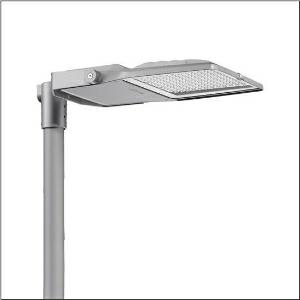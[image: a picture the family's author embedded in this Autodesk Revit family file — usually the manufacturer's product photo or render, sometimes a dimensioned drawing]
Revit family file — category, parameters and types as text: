
# Revit family: floodlight_fl_21_iq_midi___pl43_5xa7781e4a3a_24f4
name_source: partatom
category: Lighting Fixtures
units: mm (PartAtom-declared; Revit-internal decimal feet)

## family parameters
Cut with Voids When Loaded = No
Host = Face
Light Source = No
Part Type = Normal
Room Calculation Point = No
Round Connector Dimension = Use Diameter
Shared = No

## types (1)
- --- (1 x LED, 28730 lm, 208.1 W, 4000K)
    Apparent Load = 208 VA
    CIE Flux Codes = 27 78 99 100 100
    Color Rendering = 70
    Color Temperature = 4000K
    Default Elevation = 1800 mm
    Description = Floodlight FL 21 iQ midi, floodlight, primary light control with lens, of PMMA, primary optical cover: protective disc, of toughened safety glass, transparent, light distribution: PL43, light emission: direct distribution, installation type: surface-mounted, LED, High Power LED, rated luminous flux: 28.730lm, luminous efficacy: 138lm/W, light colour: 740, colour temperature: 4000K, control gear: iQ Comfort/DALI, control: optimised constant luminous flux control (CLO 2.0), Desk-Remote (wireless, voltage-free reading and setting of iQ features in the workshop via application-optimized NFC function/RFID function), Light-Fading, Smart-Wire, Night-Set, Lumen-Switch, Temp-Guard, Auto-Match, with terminal, 6-pole, mains connection: 220..240V, AC, 50/60Hz, start of lifetime: 208W, end of service life: 227W, reduction: 90W, luminaire housing, of diecast aluminium, powder-coated, Siteco® metallic grey (DB 702S), corrosivity category C5 mid according to DIN EN ISO 12944, suitable for swimming pools, chlorine-resistant, sealing non-destructively replaceable, please order mast flange separately, mast bracket, of steel, galvanised, powder-coated, Siteco® metallic grey (DB 702S), protection rating (complete): IP66, insulation class (complete): insulation class II (safety insulation), certification: CE, ENEC, VDE, protection symbol: D, impact resistance: IK08, permissible operating ambient temperature: -40..+40°C, permissible operating ambient temperature for outdoor applications: -40..+50°C, standard: DIN EN 12944, LABS conformity tested according to VDMA 24364:2018-05, packaging unit: 1 piece

Light Distribution: PL43
    Height = 76 mm
    Lamp = 1 x LED
    Lamp Light Flux = 28730 lm
    Lamp Power = 208.1 W
    Lamp count = 1
    Length = 657 mm
    Luminous efficacy = 138 lm/W
    Manufacturer = Siteco
    ModVariant = No
    Model = 5XA7781E4A3A
    Number of Poles = 1
    OnlyDefault = Yes
    Power Factor = 1
    Product Name = Floodlight FL 21 iQ midi | PL43
    Product group = floodlight | pylon annexe
    ProductGroupID = 6201
    Protection Class = Protection class II
    Protection Degree = IP 66
    RLX_Detail_Level = 1
    RLX_Emergency_Light_Flux = 0 lm
    RLX_Emergency_Type = 0
    RLX_Emergency_Type_DB = No
    RlxData = <blob elided: 153513 chars, md5=9ba9eb50>
    Socket = socket
    Standby Power = 0 W
    System Light Flux = 28730 lm
    System Power = 208 W
    Type Comments = factory setting: luminous flux: 100 % | dim-lin: 254 | 710 mA
    Type Image = l_1007123.jpg
    URL = http://relux.com
    VarID = @adj_126733
    Voltage = 0 V
    Weight = 0.00 kg
    Width = 442 mm

## geometry (parser evidence)
native form markers: Blend x4, Sweep x12
no freeform markers — native parametric forms only
